# Revit family: MI-GO
name_source: partatom
category: Pipe Accessories
revit_build: Autodesk Revit 2018 (Build: 20170223_1515(x64)
units: mm (PartAtom-declared; Revit-internal decimal feet)

## family parameters
Always vertical = Yes
Cut with Voids When Loaded = No
Part Type = Normal
Round Connector Dimension = Use Diameter
Shared = No
Work Plane-Based = No

## types (4) — shared parameters
Description = ECONOMY GREASE INTERCEPTOR
Manufacturer = MIFAB
URL = WWW.MIFAB.COM

## per-type parameters (varying)
| type | A | B | C-Pipe Offset | E-Height | Length | Width |
| MI-GO-1 | 0' - 10 3/4" | 0' - 8 3/4" | 0' - 3 3/4" | 0' - 10 1/4" | 0' - 10" | 0' - 8" |
| MI-GO-2 | 0' - 10 3/4" | 0' - 8 3/4" | 0' - 4 1/4" | 0' - 10 1/4" | 0' - 10" | 0' - 8" |
| MI-GO-3 | 1' - 6 7/8" | 0' - 10 3/4" | 0' - 4 1/2" | 1' - 3 1/2" | 1' - 6 3/8" | 0' - 10 1/4" |
| MI-GO-4 | 1' - 8 3/4" | 0' - 10 3/4" | 0' - 6" | 1' - 6" | 1' - 8 1/4" | 0' - 10 1/4" |

note: column(s) folded — value = type name in every type: Model

## geometry (parser evidence)
native form markers: Sweep x6
no freeform markers — native parametric forms only
